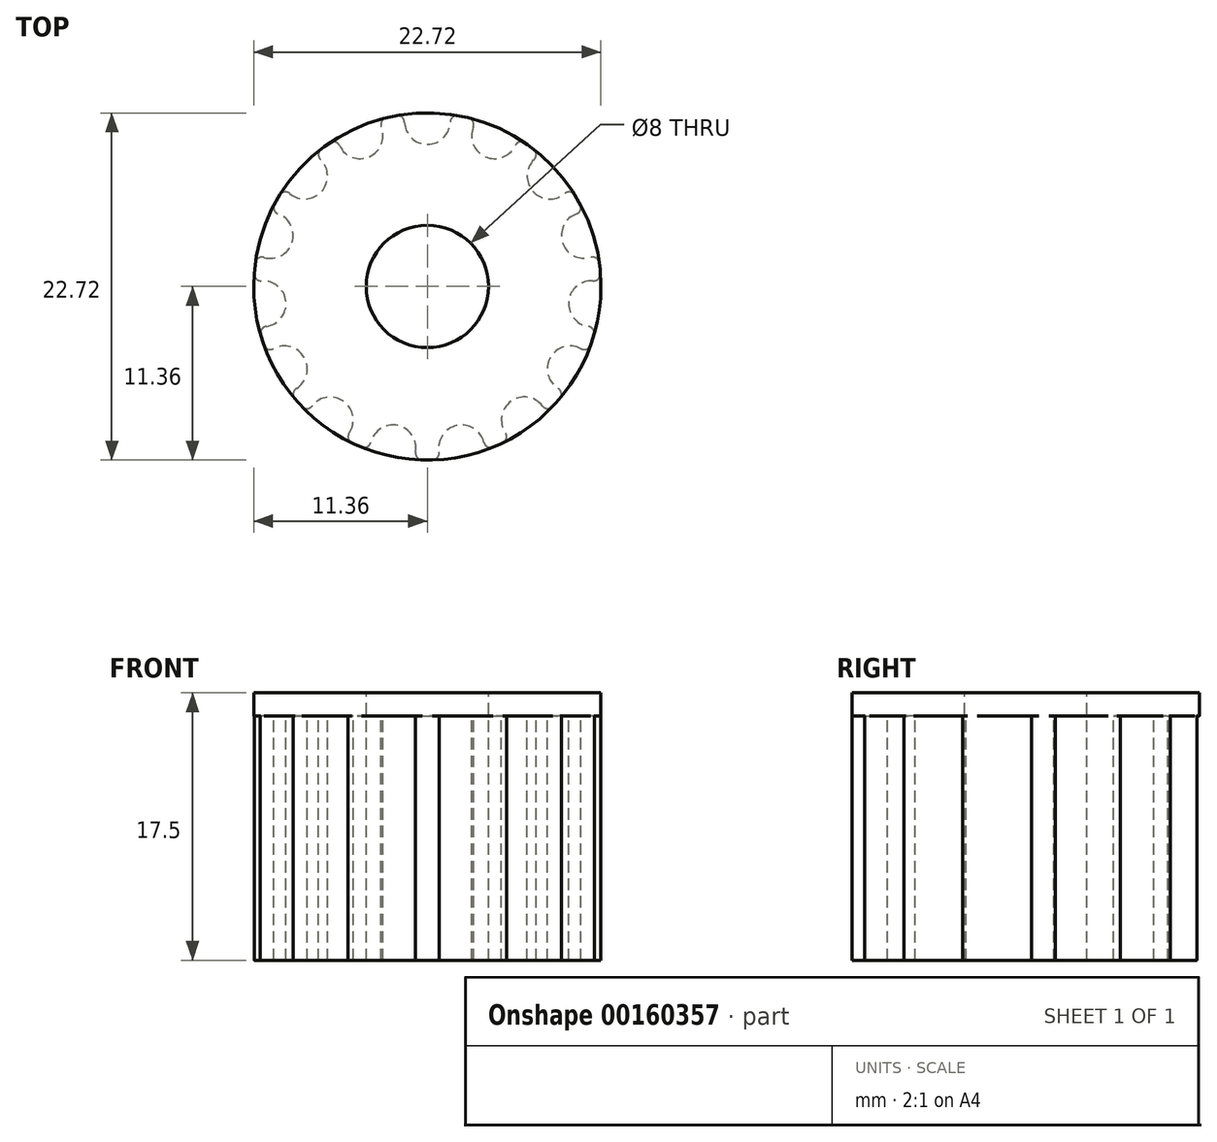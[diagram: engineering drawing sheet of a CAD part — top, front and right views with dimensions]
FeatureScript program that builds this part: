
annotation { "Feature Type Name" : "Feature", "Feature Type Description" : "" }
export const myFeature = defineFeature(function(context is Context, id is Id, definition is map)
    precondition{}
    {
        {
            assignVariable(context, id + "F0", {"name" : "Teeth", "anyValue" : 15});
        }
        {
            assignVariable(context, id + "F1", {"name" : "Width", "anyValue" : 16});
        }
        {
            var Q0;
            Q0=qCreatedBy(makeId("Top.planeOp"),FACE);
            var sketch = newSketch(context, id + "F2", { "sketchPlane" : qUnion([Q0])});
            skCircle(sketch, "E0", {"center": v(0, 0) * mm, "radius": 11.36 * mm});
            skSolve(sketch);
        }
        {
            var Q0;
            Q0=qSketchRegion(id+"F2",true);
            extrude(context, id + "F3", {"entities" : qUnion([Q0]), "depth" : (getVariable(context, 'Width')) * mm});
        }
        {
            var Q0;
            Q0=makeQuery(id+"F3.opExtrude","CAP_FACE",FACE,{"disambiguationData":[OSD([sQuery(id+"F2.wireOp",EDGE,"E0")])],"isStart":false});
            var sketch = newSketch(context, id + "F4", { "sketchPlane" : qUnion([Q0])});
            skCircle(sketch, "E1", {"center": v(0, 0) * mm, "radius": 9.3 * mm, "construction": true});
            skArc(sketch, "E2", {"start": v(-1.5, 10.75) * mm, "mid": v(0, 9.3) * mm, "end": v(1.5, 10.75) * mm});
            skArc(sketch, "E3", {"start": v(2.03, 11.18) * mm, "mid": v(0, 11.36) * mm, "end": v(-2.03, 11.18) * mm});
            skArc(sketch, "E4", {"start": v(-1.5, 10.75) * mm, "mid": v(-1.67, 11.09) * mm, "end": v(-2.03, 11.18) * mm});
            skArc(sketch, "E5", {"start": v(2.03, 11.18) * mm, "mid": v(1.67, 11.09) * mm, "end": v(1.5, 10.75) * mm});
            skSolve(sketch);
        }
        {
            var Q0;
            Q0=makeQuery(id+"F4.imprint","IMPRINT",FACE,{"disambiguationData":[TD([[makeQuery(id+"F4.imprint","IMPRINT",EDGE,{"derivedFrom":sQuery(id+"F4.wireOp",EDGE,"E2")}),1.0]])]});
            var Q1;
            Q1=makeQuery(id+"F3.opExtrude","CAP_FACE",FACE,{"disambiguationData":[OSD([sQuery(id+"F2.wireOp",EDGE,"E0")])],"isStart":true});
            extrude(context, id + "F5", {"entities" : qUnion([Q0]), "operationType" : NewBodyOperationType.REMOVE, "endBound" : BoundingType.UP_TO_SURFACE, "oppositeDirection" : true, "endBoundEntityFace" : qUnion([Q1]), "depth" : 25 * mm});
        }
        {
            var Q0;
            Q0=makeQuery(id+"F5.boolean.opBoolean","COPY",FACE,{"derivedFrom":makeQuery(id+"F5.opExtrude","SWEPT_FACE",FACE,{"disambiguationData":[OSD([sQuery(id+"F4.wireOp",EDGE,"E4")])]})});
            var Q1;
            Q1=makeQuery(id+"F5.boolean.opBoolean","COPY",FACE,{"derivedFrom":makeQuery(id+"F5.opExtrude","SWEPT_FACE",FACE,{"disambiguationData":[OSD([sQuery(id+"F4.wireOp",EDGE,"kHu0Iwj9-o4Cv-DRlk-4OjM-lw9Y4UkXsprA")])]})});
            var Q2;
            Q2=makeQuery(id+"F5.boolean.opBoolean","COPY",FACE,{"derivedFrom":makeQuery(id+"F5.opExtrude","SWEPT_FACE",FACE,{"disambiguationData":[OSD([sQuery(id+"F4.wireOp",EDGE,"E2")])]})});
            var Q3;
            Q3=makeQuery(id+"F5.boolean.opBoolean","COPY",FACE,{"derivedFrom":makeQuery(id+"F5.opExtrude","SWEPT_FACE",FACE,{"disambiguationData":[OSD([sQuery(id+"F4.wireOp",EDGE,"lCBZwTSR-BtAH-iuKv-YoZ4-wjcx4KIexOll")])]})});
            var Q4;
            Q4=makeQuery(id+"F5.boolean.opBoolean","COPY",FACE,{"derivedFrom":makeQuery(id+"F5.opExtrude","SWEPT_FACE",FACE,{"disambiguationData":[OSD([sQuery(id+"F4.wireOp",EDGE,"E5")])]})});
            var Q5;
            Q5=makeQuery(id+"F3.opExtrude","SWEPT_FACE",FACE,{"disambiguationData":[OSD([sQuery(id+"F2.wireOp",EDGE,"E0")])]});
            circularPattern(context, id + "F6", {"faces" : qUnion([Q0, Q1, Q2, Q3, Q4]), "axis" : qUnion([Q5]), "angle" : 360 * degree, "instanceCount" : getVariable(context, 'Teeth'), "equalSpace" : true, "patternType" : PatternType.FACE});
        }
        {
            var Q0;
            Q0=makeQuery(id+"F3.opExtrude","CAP_FACE",FACE,{"disambiguationData":[OSD([sQuery(id+"F2.wireOp",EDGE,"E0")])],"isStart":false});
            var sketch = newSketch(context, id + "F7", { "sketchPlane" : qUnion([Q0])});
            skCircle(sketch, "E6.0", {"center": v(0, 0) * mm, "radius": 11.36 * mm});
            skSolve(sketch);
        }
        {
            var Q0;
            Q0=qSketchRegion(id+"F7",true);
            extrude(context, id + "F8", {"entities" : qUnion([Q0]), "operationType" : NewBodyOperationType.ADD, "depth" : 1.5 * mm});
        }
        {
            var Q0;
            Q0=makeQuery(id+"F8.opExtrude","CAP_FACE",FACE,{"disambiguationData":[OSD([sQuery(id+"F7.wireOp",EDGE,"E6.0")])],"isStart":false});
            var sketch = newSketch(context, id + "F9", { "sketchPlane" : qUnion([Q0])});
            skCircle(sketch, "E7.cCircle", {"center": v(0, 0) * mm, "radius": 6.35 * mm, "construction": true});
            skLineSegment(sketch, "E7.0", {"start": v(3.67, -6.35) * mm, "end": v(-3.67, -6.35) * mm});
            skLineSegment(sketch, "E7.1", {"start": v(-3.67, -6.35) * mm, "end": v(-7.33, 0) * mm});
            skLineSegment(sketch, "E7.2", {"start": v(-7.33, 0) * mm, "end": v(-3.67, 6.35) * mm});
            skLineSegment(sketch, "E7.3", {"start": v(-3.67, 6.35) * mm, "end": v(3.67, 6.35) * mm});
            skLineSegment(sketch, "E7.4", {"start": v(3.67, 6.35) * mm, "end": v(7.33, 0) * mm});
            skLineSegment(sketch, "E7.5", {"start": v(7.33, 0) * mm, "end": v(3.67, -6.35) * mm});
            skPoint(sketch, "E7.0.midPoint", {"position": v(0, -6.35) * mm});
            skCircle(sketch, "E8", {"center": v(0, 0) * mm, "radius": 4 * mm});
            skSolve(sketch);
        }
        {
            var Q0;
            Q0=makeQuery(id+"F9.imprint","IMPRINT",FACE,{"disambiguationData":[TD([[makeQuery(id+"F9.imprint","IMPRINT",EDGE,{"derivedFrom":sQuery(id+"F9.wireOp",EDGE,"E8")}),1.0]])]});
            extrude(context, id + "F10", {"entities" : qUnion([Q0]), "operationType" : NewBodyOperationType.REMOVE, "endBound" : BoundingType.THROUGH_ALL, "oppositeDirection" : true, "depth" : 25 * mm, "offsetDistance" : 25 * mm});
        }
    });
